# Revit family: Legrand_Single_phase_isolation_transformers
name_source: partatom
category: Installations électriques
revit_build: Autodesk Revit 2018 (Build: 20170223_1515(x64)
units: mm (PartAtom-declared; Revit-internal decimal feet)

## family parameters
Basée sur le plan de construction = Non
Conserver l'orientation des annotations = Non
Cote de connecteur circulaire = Utiliser le diamètre
Couper avec des vides une fois chargée = Non
Numéro OmniClass = 23.80.00.00
Partagée = Non
Point de calcul de pièce = Non
Titre OmniClass = Electric Power and Lighting
Toujours verticalement = Oui
Type d'élément = Normal

## types (6) — shared parameters
Characteristic = Class I - IP21 - IK08
Fabricant = Legrand
General Conditions of Use = https://export.legrand.com
Modèle = Single phase isolation transformers
Primary voltage = 230V - 400V
Secondary voltage = 115V - 230V
URL = www.legrand.com

## per-type parameters (varying)
| type | 042500 | 042501 | 042502 | 042503 | 042504, 042505 | Insulating | Primary Cable Section | Secondary cable section | Ucc (%) | dimension A | dimension B | dimension C | empty loss | fixing F | fixing G | fixing diameter | max totaly loss | power | weight |
| single phase transformer 042503 | Non | Non | Non | Oui | Non | class H | 10 mm² | 16 mm² | 5.2 | 300 mm  [stored 0.984252 ft] | 390 mm  [stored 1.27953 ft] | 230 mm  [stored 0.754593 ft] | 77 W | 280 mm  [stored 0.918635 ft] | 130 mm  [stored 0.426509 ft] | 9 mm  [stored 0.0295276 ft] | 297 W | 4 kVA | 39.00 kg |
| single phase transformer 042500 | Oui | Non | Non | Non | Non | class B | 6mm² | 6 mm² | 3.8 | 230 mm  [stored 0.754593 ft] | 270 mm  [stored 0.885827 ft] | 253 mm  [stored 0.830052 ft] | 46 W | 210 mm  [stored 0.688976 ft] | 135 mm  [stored 0.442913 ft] | 7 mm  [stored 0.0229659 ft] | 84 W | 1 kVA | 25.00 kg |
| single phase transformer 042501 | Non | Oui | Non | Non | Non | class B | 6 mm² | 6 mm² | 2.7 | 250 mm  [stored 0.82021 ft] | 270 mm  [stored 0.885827 ft] | 253 mm  [stored 0.830052 ft] | 65 W | 230 mm  [stored 0.754593 ft] | 134 mm | 7 mm  [stored 0.0229659 ft] | 108 W | 2 kVA | 26.00 kg |
| single phase transformer 042502 | Non | Non | Oui | Non | Non | class B | 10 mm² | 10 mm² | 2.1 | 320 mm  [stored 1.04987 ft] | 330 mm | 253 mm  [stored 0.830052 ft] | 89 W | 300 mm  [stored 0.984252 ft] | 111 mm | 9 mm  [stored 0.0295276 ft] | 139 W | 3 kVA | 36.00 kg |
| single phase transformer 042504 | Non | Non | Non | Non | Oui | class H | 16 mm² | 16 mm² | 4.1 | 340 mm  [stored 1.11549 ft] | 410 mm  [stored 1.34514 ft] | 320 mm  [stored 1.04987 ft] | 120 W | 320 mm  [stored 1.04987 ft] | 130 mm  [stored 0.426509 ft] | 9 mm  [stored 0.0295276 ft] | 390 W | 6 kVA | 49.00 kg |
| single phase transformer 042505 | Non | Non | Non | Non | Oui | class H | 16 mm² | 35 mm² | 3.9 | 340 mm  [stored 1.11549 ft] | 410 mm  [stored 1.34514 ft] | 320 mm  [stored 1.04987 ft] | 162 W | 320 mm  [stored 1.04987 ft] | 180 mm  [stored 0.590551 ft] | 9 mm  [stored 0.0295276 ft] | 554 W | 10 kVA | 78.00 kg |

note: [stored X ft] marks values corroborated as IEEE doubles in the binary element streams (Revit-internal decimal feet)
